# Revit family: LVPTALAS-DC01
name_source: partatom
category: Aparatos sanitarios
units: mm (PartAtom-declared; Revit-internal decimal feet)

## family parameters
Activar corte en vistas = No
Compartido = No
Corte con vacíos al cargar = No
Cota de conector redondo = Usar diámetro
Mantener orientación de anotación = No
Número OmniClass = 23.45.00.00
Punto de cálculo de habitación = No
Se basa en plano de trabajo = No
Siempre vertical = Sí
Tipo de pieza = Normal
Título OmniClass = Sanitary, Laundry, and Cleaning Equipment

## types (1)
- LVPTALAS-DC01
    Alto = 37"
    Ancho = 18"
    Cerámica de alto brillo = Cerámica
    Comentarios de tipo = Monomando sin Contra Deco y Lavabo Talas
    Descripción = Monomando sin Contra Deco y Lavabo Talas
    Elevación por defecto = 0"
    Fabricante = PROYECTA
    Features = Monomando para lavabo sin contra, con
cartucho de 35 mm.
Discos cerámicos de alta dureza que extienden
y aseguran la vida del cartucho sin fugas.
Sin contra.
Fácil instalación y mantenimiento.
Lavabo con pedestal y rebosadero.
Fácil instalación y mantenimiento.
    Imagen de tipo = LVPTALAS-DC01.png
    Largo = 15"
    Modelo = LVPTALAS-DC01

## geometry (parser evidence)
native form markers: Sweep x3
no freeform markers — native parametric forms only
